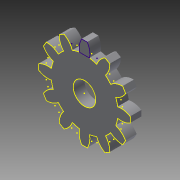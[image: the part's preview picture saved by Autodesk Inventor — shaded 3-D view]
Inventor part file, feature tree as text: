
AUTODESK INVENTOR PART (.ipt)
format: ipt  version: 2013 (Build 170138000, 138)  size: 203,264 bytes
history: native  units: in
note: dims shown in document units (in); Inventor stores cm internally (conversion verified against a paired STEP export)
features: sketch x3, extrude x2
ambient origin geometry x8: Origin, YZ Plane, XZ Plane, XY Plane, X Axis, Y Axis, Z Axis, Center Point
bodies: Solid1 (feature_tree)
feature tree (5):
  extrude  "Extrusion1"  Depth=4.7244in TaperAngle=360.0deg
  extrude  "Extrusion2"  Depth=0.071in
  sketch  "Sketch3"  dims[d8=0.1in d9=0.0625in d10=0.0in d11=0.0413in d12=0.125in d14=0.0625in d15=0.0in]
  sketch  "Sketch1"  dims[d0=0.0312in d2=4.7244in d4=360.0deg]
  sketch  "Sketch2"  dims[d6=0.5497in d7=0.071in]
